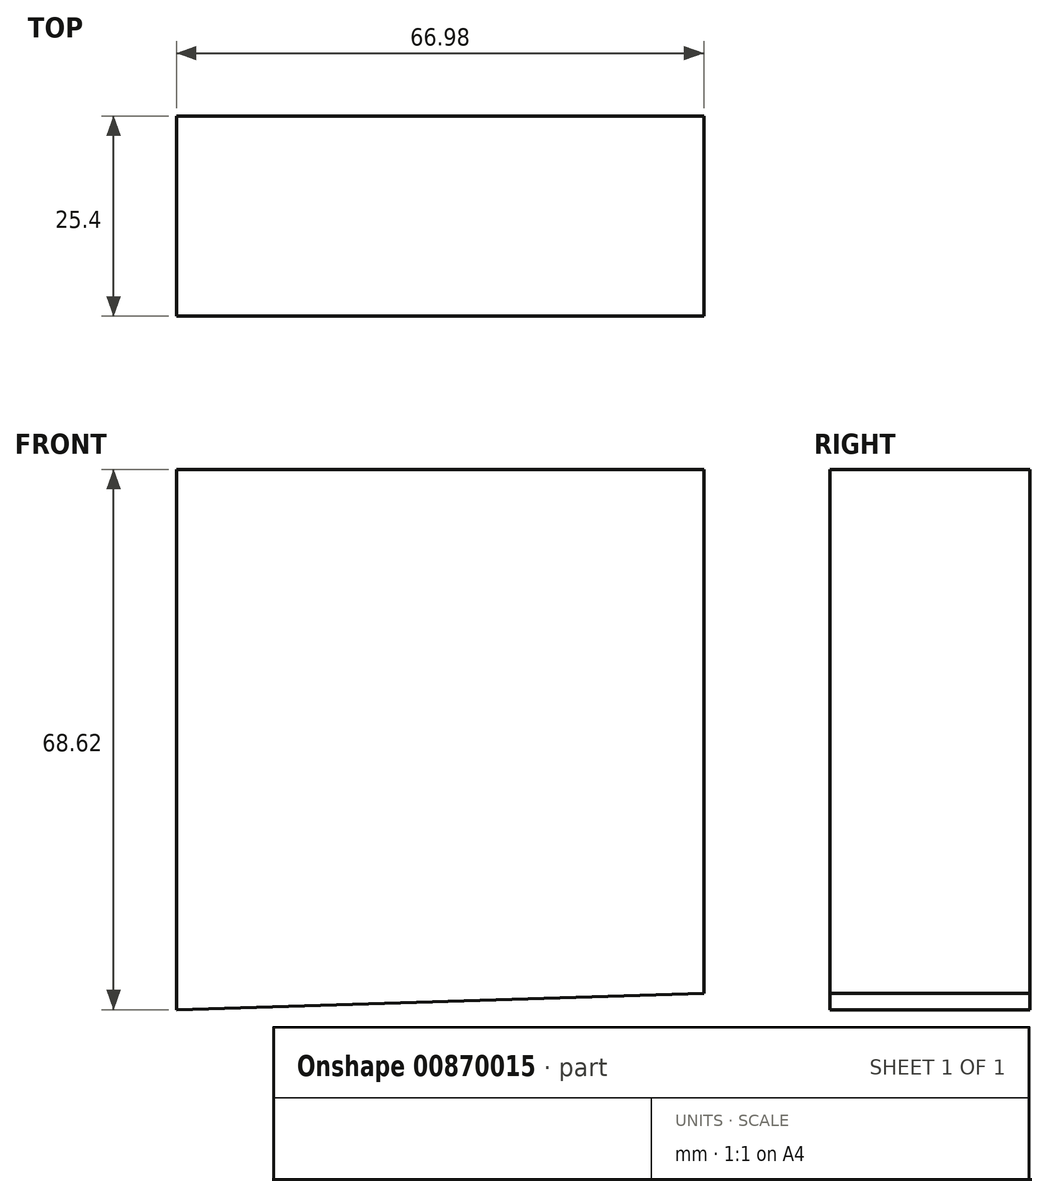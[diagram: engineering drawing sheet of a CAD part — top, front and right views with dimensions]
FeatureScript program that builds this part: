
annotation { "Feature Type Name" : "Feature", "Feature Type Description" : "" }
export const myFeature = defineFeature(function(context is Context, id is Id, definition is map)
    precondition{}
    {
        {
            var Q0;
            Q0=qCreatedBy(makeId("Front.planeOp"),FACE);
            var sketch = newSketch(context, id + "F0", { "sketchPlane" : qUnion([Q0])});
            skLineSegment(sketch, "E0", {"start": v(-36.48, -38.83) * mm, "end": v(-36.48, 29.8) * mm});
            skLineSegment(sketch, "E1", {"start": v(-36.48, 29.8) * mm, "end": v(30.5, 29.8) * mm});
            skLineSegment(sketch, "E2", {"start": v(30.5, 29.8) * mm, "end": v(30.5, -36.78) * mm});
            skLineSegment(sketch, "E3", {"start": v(30.5, -36.78) * mm, "end": v(-36.48, -38.83) * mm});
            skSolve(sketch);
        }
        {
            var Q0;
            Q0 = qSketchRegion(id + "F0", true);
            extrude(context, id + "F1", {"entities" : qUnion([Q0]), "depth" : 25.4 * mm, "offsetDistance" : 25.4 * mm});
        }
    });
